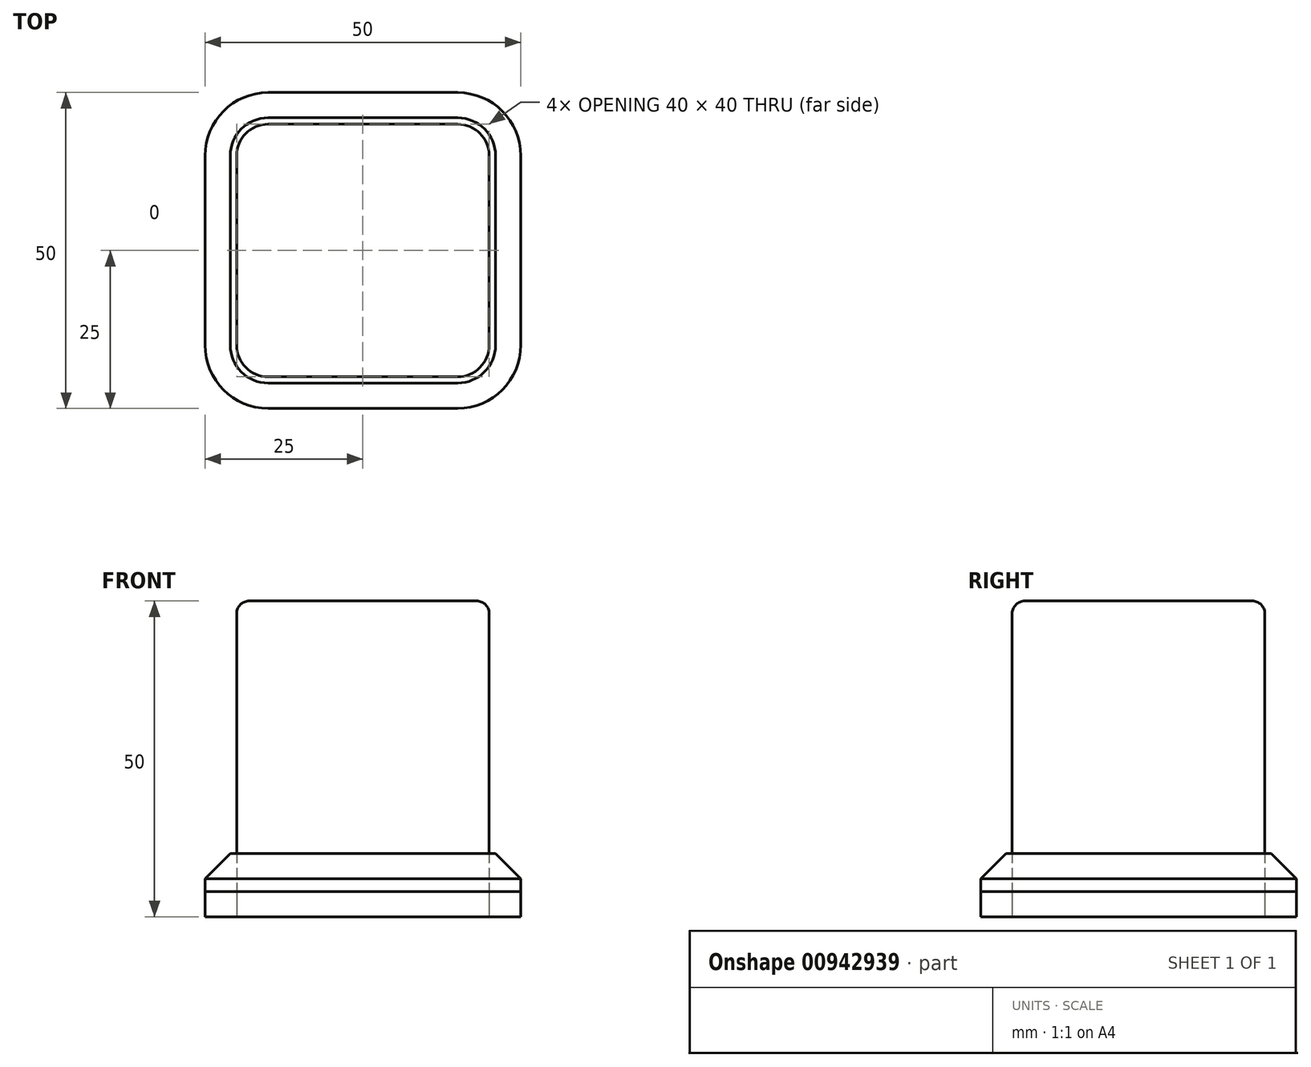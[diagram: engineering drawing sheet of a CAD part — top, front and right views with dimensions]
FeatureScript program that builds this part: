
annotation { "Feature Type Name" : "Feature", "Feature Type Description" : "" }
export const myFeature = defineFeature(function(context is Context, id is Id, definition is map)
    precondition{}
    {
        {
            var Q0;
            Q0=qCreatedBy(makeId("Top.planeOp"),FACE);
            var sketch = newSketch(context, id + "F0", { "sketchPlane" : qUnion([Q0])});
            skLineSegment(sketch, "E0.bottom", {"start": v(10, 0) * mm, "end": v(40, 0) * mm});
            skLineSegment(sketch, "E0.top", {"start": v(10, 50) * mm, "end": v(40, 50) * mm});
            skLineSegment(sketch, "E0.left", {"start": v(0, 10) * mm, "end": v(0, 40) * mm});
            skLineSegment(sketch, "E0.right", {"start": v(50, 10) * mm, "end": v(50, 40) * mm});
            skPoint(sketch, "E1.visualSharp", {"position": v(0, 50) * mm});
            skArc(sketch, "E1.filletArc", {"start": v(10, 50) * mm, "mid": v(2.93, 47.07) * mm, "end": v(0, 40) * mm});
            skPoint(sketch, "E2.visualSharp", {"position": v(50, 50) * mm});
            skArc(sketch, "E2.filletArc", {"start": v(50, 40) * mm, "mid": v(47.07, 47.07) * mm, "end": v(40, 50) * mm});
            skPoint(sketch, "E3.visualSharp", {"position": v(50, 0) * mm});
            skArc(sketch, "E3.filletArc", {"start": v(40, 0) * mm, "mid": v(47.07, 2.93) * mm, "end": v(50, 10) * mm});
            skPoint(sketch, "E4.visualSharp", {"position": v(0, 0) * mm});
            skArc(sketch, "E4.filletArc", {"start": v(0, 10) * mm, "mid": v(2.93, 2.93) * mm, "end": v(10, 0) * mm});
            skLineSegment(sketch, "E5.bottom", {"start": v(10, 5) * mm, "end": v(40, 5) * mm});
            skLineSegment(sketch, "E5.top", {"start": v(10, 45) * mm, "end": v(40, 45) * mm});
            skLineSegment(sketch, "E5.left", {"start": v(5, 10) * mm, "end": v(5, 40) * mm});
            skLineSegment(sketch, "E5.right", {"start": v(45, 10) * mm, "end": v(45, 40) * mm});
            skPoint(sketch, "E6.visualSharp", {"position": v(5, 45) * mm});
            skArc(sketch, "E6.filletArc", {"start": v(10, 45) * mm, "mid": v(6.46, 43.54) * mm, "end": v(5, 40) * mm});
            skPoint(sketch, "E7.visualSharp", {"position": v(45, 45) * mm});
            skArc(sketch, "E7.filletArc", {"start": v(45, 40) * mm, "mid": v(43.54, 43.54) * mm, "end": v(40, 45) * mm});
            skPoint(sketch, "E8.visualSharp", {"position": v(45, 5) * mm});
            skArc(sketch, "E8.filletArc", {"start": v(40, 5) * mm, "mid": v(43.54, 6.46) * mm, "end": v(45, 10) * mm});
            skPoint(sketch, "E9.visualSharp", {"position": v(5, 5) * mm});
            skArc(sketch, "E9.filletArc", {"start": v(5, 10) * mm, "mid": v(6.46, 6.46) * mm, "end": v(10, 5) * mm});
            skSolve(sketch);
        }
        {
            var Q0;
            Q0=makeQuery(id+"F0.imprint","IMPRINT",FACE,{"disambiguationData":[TD([[makeQuery(id+"F0.imprint","IMPRINT",EDGE,{"derivedFrom":sQuery(id+"F0.wireOp",EDGE,"E0.bottom")}),1.0]])]});
            extrude(context, id + "F1", {"entities" : qUnion([Q0]), "depth" : 4 * mm, "offsetDistance" : 25 * mm});
        }
        {
            var Q0;
            Q0 = qSketchRegion(id + "F0", true);
            extrude(context, id + "F2", {"entities" : qUnion([Q0]), "depth" : 10 * mm, "offsetDistance" : 25 * mm, "hasSecondDirection" : true, "secondDirectionOppositeDirection" : true, "secondDirectionDepth" : -4 * mm});
        }
        {
            var Q0;
            Q0=makeQuery(id+"F2.opExtrude","CAP_EDGE",EDGE,{"disambiguationData":[OSD([sQuery(id+"F0.wireOp",EDGE,"E0.right")])],"isStart":false});
            chamfer(context, id + "F3", {"entities" : qUnion([Q0]), "width" : 4 * mm, "tangentPropagation" : true});
        }
        {
            var Q0;
            Q0=makeQuery(id+"F0.imprint","IMPRINT",FACE,{"disambiguationData":[TD([[makeQuery(id+"F0.imprint","IMPRINT",EDGE,{"derivedFrom":sQuery(id+"F0.wireOp",EDGE,"E5.bottom")}),1.0]])]});
            extrude(context, id + "F4", {"entities" : qUnion([Q0]), "depth" : 50 * mm, "offsetDistance" : 25 * mm});
        }
        {
            var Q0;
            Q0=makeQuery(id+"F4.opExtrude","CAP_EDGE",EDGE,{"disambiguationData":[OSD([sQuery(id+"F0.wireOp",EDGE,"E5.top")])],"isStart":false});
            fillet(context, id + "F5", {"entities" : qUnion([Q0]), "radius" : 2 * mm, "tangentPropagation" : true, "allowEdgeOverflow" : false});
        }
    });
